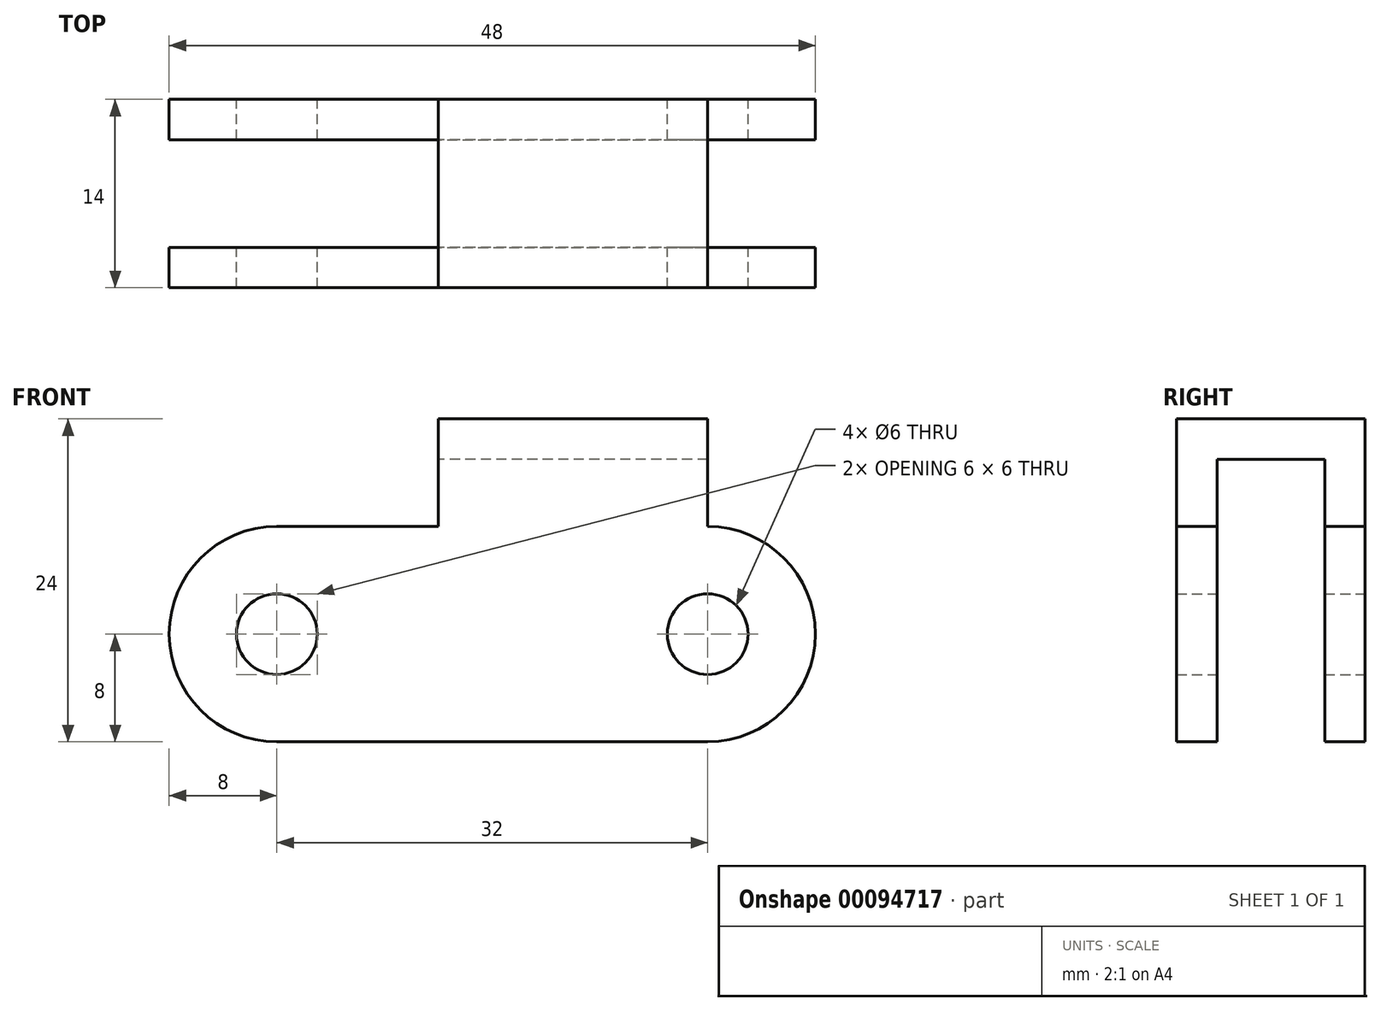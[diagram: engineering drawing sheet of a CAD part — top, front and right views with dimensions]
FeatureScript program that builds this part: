
annotation { "Feature Type Name" : "Feature", "Feature Type Description" : "" }
export const myFeature = defineFeature(function(context is Context, id is Id, definition is map)
    precondition{}
    {
        {
            var Q0;
            Q0=qCreatedBy(makeId("Front.planeOp"),FACE);
            var sketch = newSketch(context, id + "F0", { "sketchPlane" : qUnion([Q0])});
            skArc(sketch, "E0", {"start": v(0, -8) * mm, "mid": v(8, 0) * mm, "end": v(0, 8) * mm});
            skLineSegment(sketch, "E1", {"start": v(0, 8) * mm, "end": v(-32, 8) * mm});
            skLineSegment(sketch, "E2", {"start": v(0, 0) * mm, "end": v(-32, 0) * mm});
            skCircle(sketch, "E3", {"center": v(0, 0) * mm, "radius": 3 * mm});
            skLineSegment(sketch, "E4", {"start": v(0, -8) * mm, "end": v(-32, -8) * mm});
            skCircle(sketch, "E5", {"center": v(-32, 0) * mm, "radius": 3 * mm});
            skArc(sketch, "E6", {"start": v(-32, 8) * mm, "mid": v(-40, 0) * mm, "end": v(-32, -8) * mm});
            skLineSegment(sketch, "E7", {"start": v(0, 8) * mm, "end": v(0, 16) * mm});
            skLineSegment(sketch, "E8", {"start": v(0, 16) * mm, "end": v(-20, 16) * mm});
            skLineSegment(sketch, "E9", {"start": v(-20, 16) * mm, "end": v(-20, 8) * mm});
            skSolve(sketch);
        }
        {
            var Q0;
            Q0 = qSketchRegion(id + "F0", true);
            extrude(context, id + "F1", {"entities" : qUnion([Q0]), "endBound" : BoundingType.SYMMETRIC, "depth" : 14 * mm});
        }
        {
            var Q0;
            Q0=qCreatedBy(makeId("Right.planeOp"),FACE);
            var sketch = newSketch(context, id + "F2", { "sketchPlane" : qUnion([Q0])});
            skLineSegment(sketch, "E10.bottom", {"start": v(-4, 13) * mm, "end": v(4, 13) * mm});
            skLineSegment(sketch, "E10.top", {"start": v(-4, -13) * mm, "end": v(4, -13) * mm});
            skLineSegment(sketch, "E10.left", {"start": v(-4, 13) * mm, "end": v(-4, -13) * mm});
            skLineSegment(sketch, "E10.right", {"start": v(4, 13) * mm, "end": v(4, -13) * mm});
            skPoint(sketch, "E10.middle", {"position": v(0, 0) * mm});
            skSolve(sketch);
        }
        {
            var Q0;
            Q0=makeQuery(id+"F2.imprint","IMPRINT",FACE,{"disambiguationData":[TD([[makeQuery(id+"F2.imprint","IMPRINT",EDGE,{"derivedFrom":sQuery(id+"F2.wireOp",EDGE,"E10.bottom")}),-1.0]])]});
            extrude(context, id + "F3", {"entities" : qUnion([Q0]), "operationType" : NewBodyOperationType.REMOVE, "endBound" : BoundingType.SYMMETRIC, "depth" : 100.06 * mm});
        }
    });
